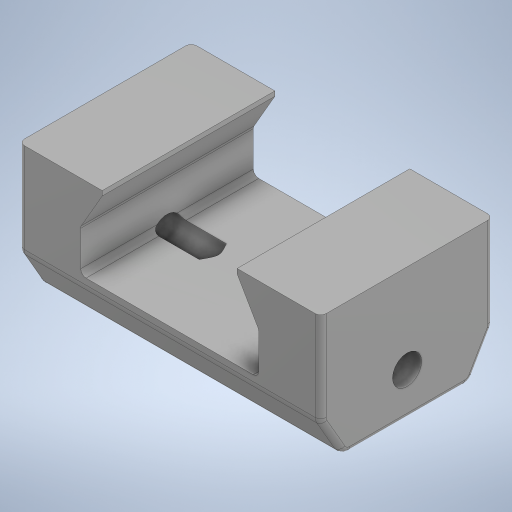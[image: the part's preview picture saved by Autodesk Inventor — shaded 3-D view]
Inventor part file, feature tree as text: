
AUTODESK INVENTOR PART (.ipt)
format: ipt  version: 2023.1 (Build 271208000, 208)  size: 668,672 bytes
history: native  units: mm
features: other x1, fillet x1
ambient origin geometry x8: Origin, YZ Plane, XZ Plane, XY Plane, X Axis, Y Axis, Z Axis, Center Point
bodies: Solid1 (feature_tree)
feature tree (2):
  other  "39300C_TXM-Linear Slide Bushing.STEP"
  fillet  "Fillet5"  [1 undecoded]
note: 1 required parameter value undecoded (feature->parameter linkage not recoverable at this tier; creation-order binding heuristic only, values carry confidence <= 0.55)
